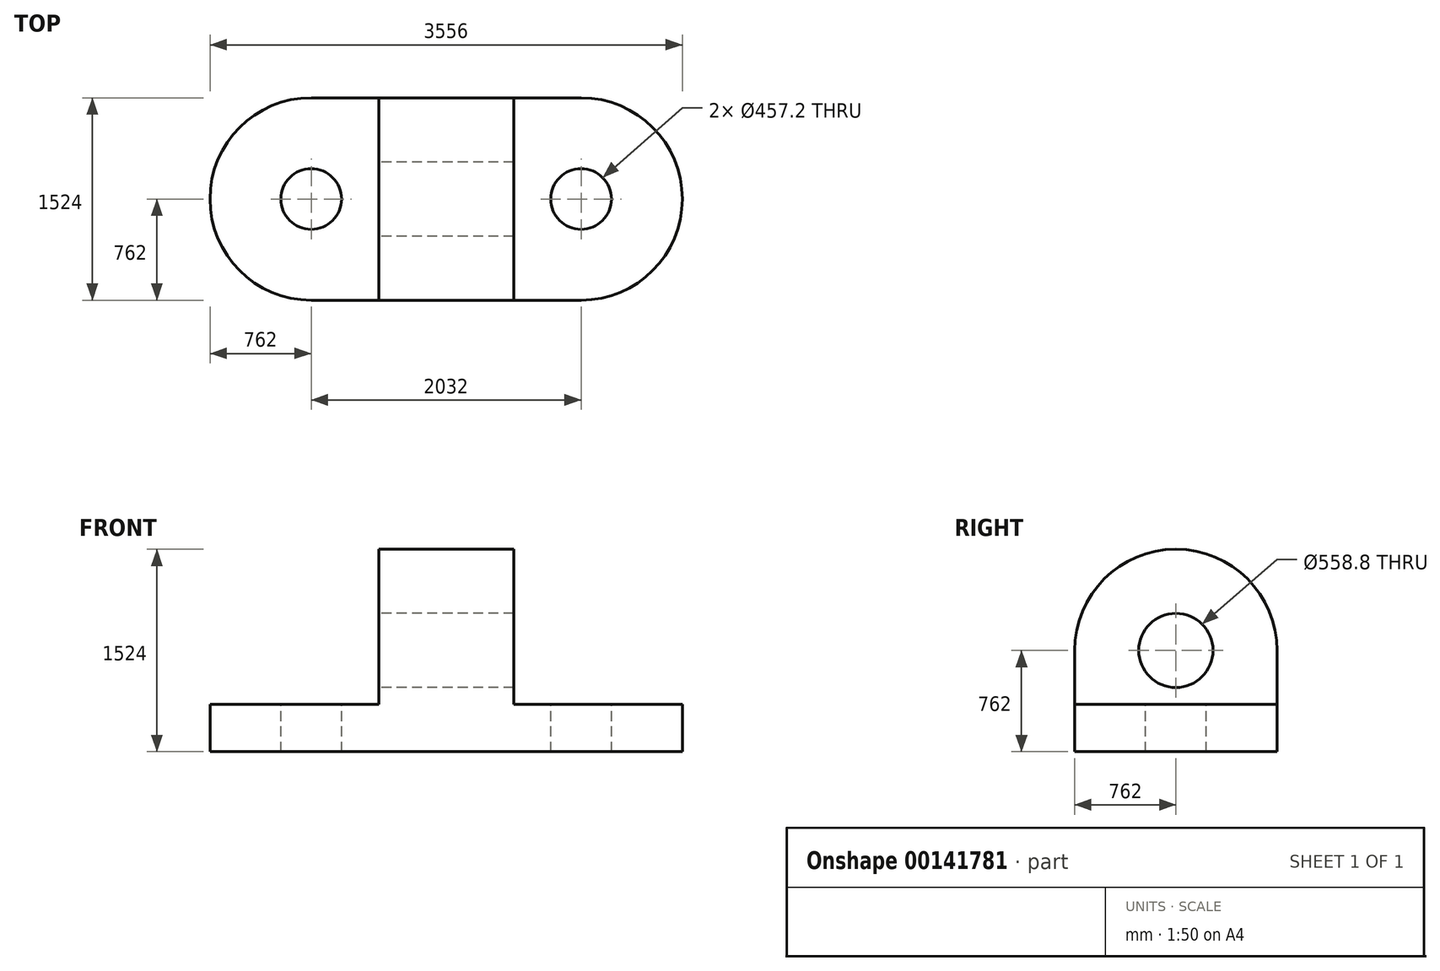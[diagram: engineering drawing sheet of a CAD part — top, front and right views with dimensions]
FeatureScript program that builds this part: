
annotation { "Feature Type Name" : "Feature", "Feature Type Description" : "" }
export const myFeature = defineFeature(function(context is Context, id is Id, definition is map)
    precondition{}
    {
        {
            var Q0;
            Q0=qCreatedBy(makeId("Top.planeOp"),FACE);
            var sketch = newSketch(context, id + "F0", { "sketchPlane" : qUnion([Q0])});
            skLineSegment(sketch, "E0.bottom", {"start": v(0, 0) * mm, "end": v(-3556, 0) * mm});
            skLineSegment(sketch, "E0.top", {"start": v(0, 1524) * mm, "end": v(-3556, 1524) * mm});
            skLineSegment(sketch, "E0.left", {"start": v(0, 0) * mm, "end": v(0, 1524) * mm});
            skLineSegment(sketch, "E0.right", {"start": v(-3556, 0) * mm, "end": v(-3556, 1524) * mm});
            skSolve(sketch);
        }
        {
            var Q0;
            Q0 = qSketchRegion(id + "F0", true);
            extrude(context, id + "F1", {"entities" : qUnion([Q0]), "depth" : 355.6 * mm});
        }
        {
            var Q0;
            Q0=makeQuery(id+"F1.opExtrude","CAP_FACE",FACE,{"disambiguationData":[OSD([sQuery(id+"F0.wireOp",EDGE,"E0.bottom"),sQuery(id+"F0.wireOp",EDGE,"E0.top"),sQuery(id+"F0.wireOp",EDGE,"E0.left"),sQuery(id+"F0.wireOp",EDGE,"E0.right")])],"isStart":false});
            var sketch = newSketch(context, id + "F2", { "sketchPlane" : qUnion([Q0])});
            skLineSegment(sketch, "E1.bottom", {"start": v(-2286, 0) * mm, "end": v(-1270, 0) * mm});
            skLineSegment(sketch, "E1.top", {"start": v(-2286, 1524) * mm, "end": v(-1270, 1524) * mm});
            skLineSegment(sketch, "E1.left", {"start": v(-2286, 0) * mm, "end": v(-2286, 1524) * mm});
            skLineSegment(sketch, "E1.right", {"start": v(-1270, 0) * mm, "end": v(-1270, 1524) * mm});
            skSolve(sketch);
        }
        {
            var Q0;
            Q0=makeQuery(id+"F2.imprint","IMPRINT",FACE,{"disambiguationData":[TD([[makeQuery(id+"F2.imprint","IMPRINT",EDGE,{"derivedFrom":sQuery(id+"F2.wireOp",EDGE,"E1.bottom")}),-1.0]])]});
            extrude(context, id + "F3", {"entities" : qUnion([Q0]), "operationType" : NewBodyOperationType.ADD, "depth" : 1168.4 * mm});
        }
        {
            var Q0;
            Q0=makeQuery(id+"F3.opExtrude","CAP_EDGE",EDGE,{"disambiguationData":[OSD([sQuery(id+"F2.wireOp",EDGE,"E1.bottom")])],"isStart":false});
            var Q1;
            Q1=makeQuery(id+"F1.opExtrude","SWEPT_EDGE",EDGE,{"disambiguationData":[OSD([sQuery(id+"F0.wireOp",EDGE,"E0.bottom"),sQuery(id+"F0.wireOp",EDGE,"E0.left")])]});
            var Q2;
            Q2=makeQuery(id+"F1.opExtrude","SWEPT_EDGE",EDGE,{"disambiguationData":[OSD([sQuery(id+"F0.wireOp",EDGE,"E0.top"),sQuery(id+"F0.wireOp",EDGE,"E0.left")])]});
            var Q3;
            Q3=makeQuery(id+"F1.opExtrude","SWEPT_EDGE",EDGE,{"disambiguationData":[OSD([sQuery(id+"F0.wireOp",EDGE,"E0.bottom"),sQuery(id+"F0.wireOp",EDGE,"E0.right")])]});
            var Q4;
            Q4=makeQuery(id+"F1.opExtrude","SWEPT_EDGE",EDGE,{"disambiguationData":[OSD([sQuery(id+"F0.wireOp",EDGE,"E0.top"),sQuery(id+"F0.wireOp",EDGE,"E0.right")])]});
            var Q5;
            Q5=makeQuery(id+"F3.opExtrude","CAP_EDGE",EDGE,{"disambiguationData":[OSD([sQuery(id+"F2.wireOp",EDGE,"E1.top")])],"isStart":false});
            fillet(context, id + "F4", {"entities" : qUnion([Q0, Q1, Q2, Q3, Q4, Q5]), "radius" : 762 * mm, "tangentPropagation" : true, "allowEdgeOverflow" : false});
        }
        {
            var Q0;
            Q0=makeQuery(id+"F3.opExtrude","SWEPT_FACE",FACE,{"disambiguationData":[OSD([sQuery(id+"F2.wireOp",EDGE,"E1.left")])]});
            var sketch = newSketch(context, id + "F5", { "sketchPlane" : qUnion([Q0])});
            skCircle(sketch, "E2", {"center": v(-762, 762) * mm, "radius": 279.4 * mm});
            skSolve(sketch);
        }
        {
            var Q0;
            Q0=makeQuery(id+"F5.imprint","IMPRINT",FACE,{"disambiguationData":[TD([[makeQuery(id+"F5.imprint","IMPRINT",EDGE,{"derivedFrom":sQuery(id+"F5.wireOp",EDGE,"E2")}),1.0]])]});
            extrude(context, id + "F6", {"entities" : qUnion([Q0]), "operationType" : NewBodyOperationType.REMOVE, "oppositeDirection" : true, "depth" : 1016 * mm});
        }
        {
            var Q0;
            {var subQ0=sQuery(id+"F0.wireOp",EDGE,"E0.left");var subQ1=sQuery(id+"F0.wireOp",EDGE,"E0.top");var subQ2=sQuery(id+"F0.wireOp",EDGE,"E0.bottom");Q0=makeQuery(id+"F3.boolean.opBoolean","SPLIT",FACE,{"disambiguationData":[TD([makeQuery(id+"F1.opExtrude","SWEPT_FACE",FACE,{"disambiguationData":[OSD([subQ0])]})])],"derivedFrom":makeQuery(id+"F1.opExtrude","CAP_FACE",FACE,{"disambiguationData":[OSD([subQ2,subQ1,subQ0,sQuery(id+"F0.wireOp",EDGE,"E0.right")])],"isStart":false})});}
            var sketch = newSketch(context, id + "F7", { "sketchPlane" : qUnion([Q0])});
            skCircle(sketch, "E3", {"center": v(-762, 762) * mm, "radius": 228.6 * mm});
            skSolve(sketch);
        }
        {
            var Q0;
            Q0=makeQuery(id+"F7.imprint","IMPRINT",FACE,{"disambiguationData":[TD([[makeQuery(id+"F7.imprint","IMPRINT",EDGE,{"derivedFrom":sQuery(id+"F7.wireOp",EDGE,"E3")}),1.0]])]});
            extrude(context, id + "F8", {"entities" : qUnion([Q0]), "operationType" : NewBodyOperationType.REMOVE, "oppositeDirection" : true, "depth" : 355.6 * mm});
        }
        {
            var Q0;
            {var subQ0=sQuery(id+"F0.wireOp",EDGE,"E0.right");var subQ1=sQuery(id+"F0.wireOp",EDGE,"E0.top");var subQ2=sQuery(id+"F0.wireOp",EDGE,"E0.bottom");Q0=makeQuery(id+"F3.boolean.opBoolean","SPLIT",FACE,{"disambiguationData":[TD([makeQuery(id+"F1.opExtrude","SWEPT_FACE",FACE,{"disambiguationData":[OSD([subQ0])]})])],"derivedFrom":makeQuery(id+"F1.opExtrude","CAP_FACE",FACE,{"disambiguationData":[OSD([subQ2,subQ1,sQuery(id+"F0.wireOp",EDGE,"E0.left"),subQ0])],"isStart":false})});}
            var sketch = newSketch(context, id + "F9", { "sketchPlane" : qUnion([Q0])});
            skCircle(sketch, "E4", {"center": v(-2794, 762) * mm, "radius": 228.6 * mm});
            skSolve(sketch);
        }
        {
            var Q0;
            Q0=makeQuery(id+"F9.imprint","IMPRINT",FACE,{"disambiguationData":[TD([[makeQuery(id+"F9.imprint","IMPRINT",EDGE,{"derivedFrom":sQuery(id+"F9.wireOp",EDGE,"E4")}),1.0]])]});
            extrude(context, id + "F10", {"entities" : qUnion([Q0]), "operationType" : NewBodyOperationType.REMOVE, "oppositeDirection" : true, "depth" : 355.6 * mm});
        }
    });
